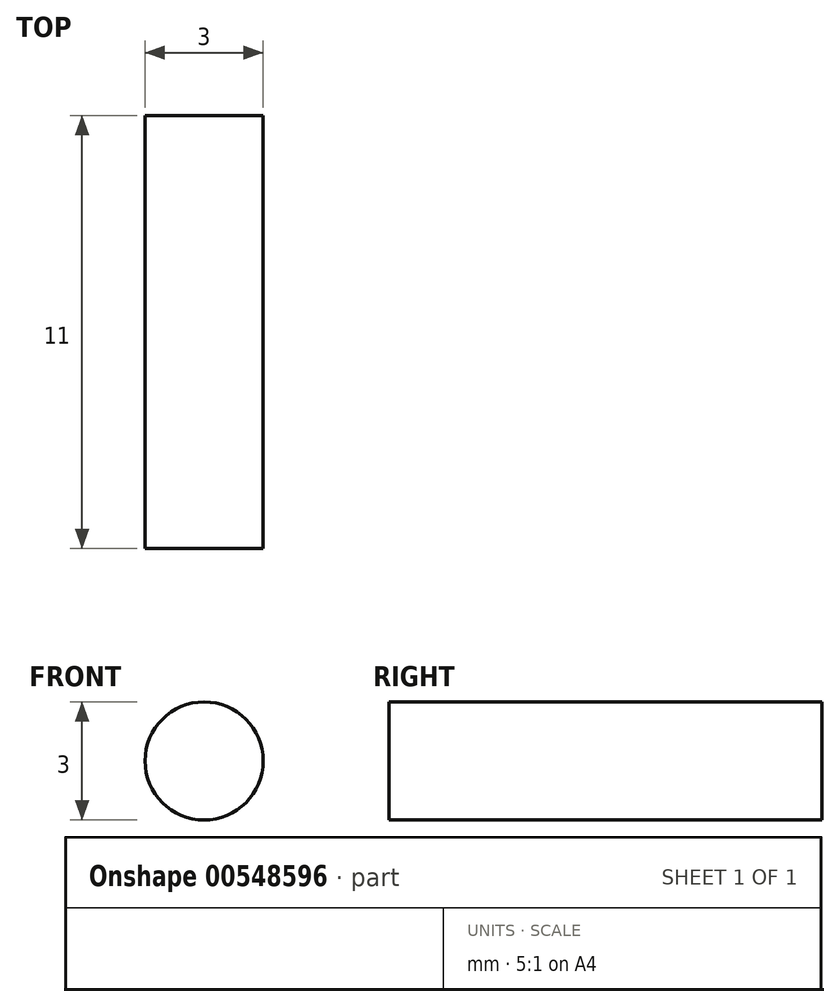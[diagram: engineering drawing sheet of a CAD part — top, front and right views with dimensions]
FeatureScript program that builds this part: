
annotation { "Feature Type Name" : "Feature", "Feature Type Description" : "" }
export const myFeature = defineFeature(function(context is Context, id is Id, definition is map)
    precondition{}
    {
        {
            var Q0;
            Q0=qCreatedBy(makeId("Front.planeOp"),FACE);
            var sketch = newSketch(context, id + "F0", { "sketchPlane" : qUnion([Q0])});
            skCircle(sketch, "E0", {"center": v(0, 0) * mm, "radius": 1.5 * mm});
            skSolve(sketch);
        }
        {
            var Q0;
            Q0 = qSketchRegion(id + "F0", true);
            extrude(context, id + "F1", {"entities" : qUnion([Q0]), "endBound" : BoundingType.SYMMETRIC, "depth" : 11 * mm, "offsetDistance" : 25 * mm});
        }
    });
